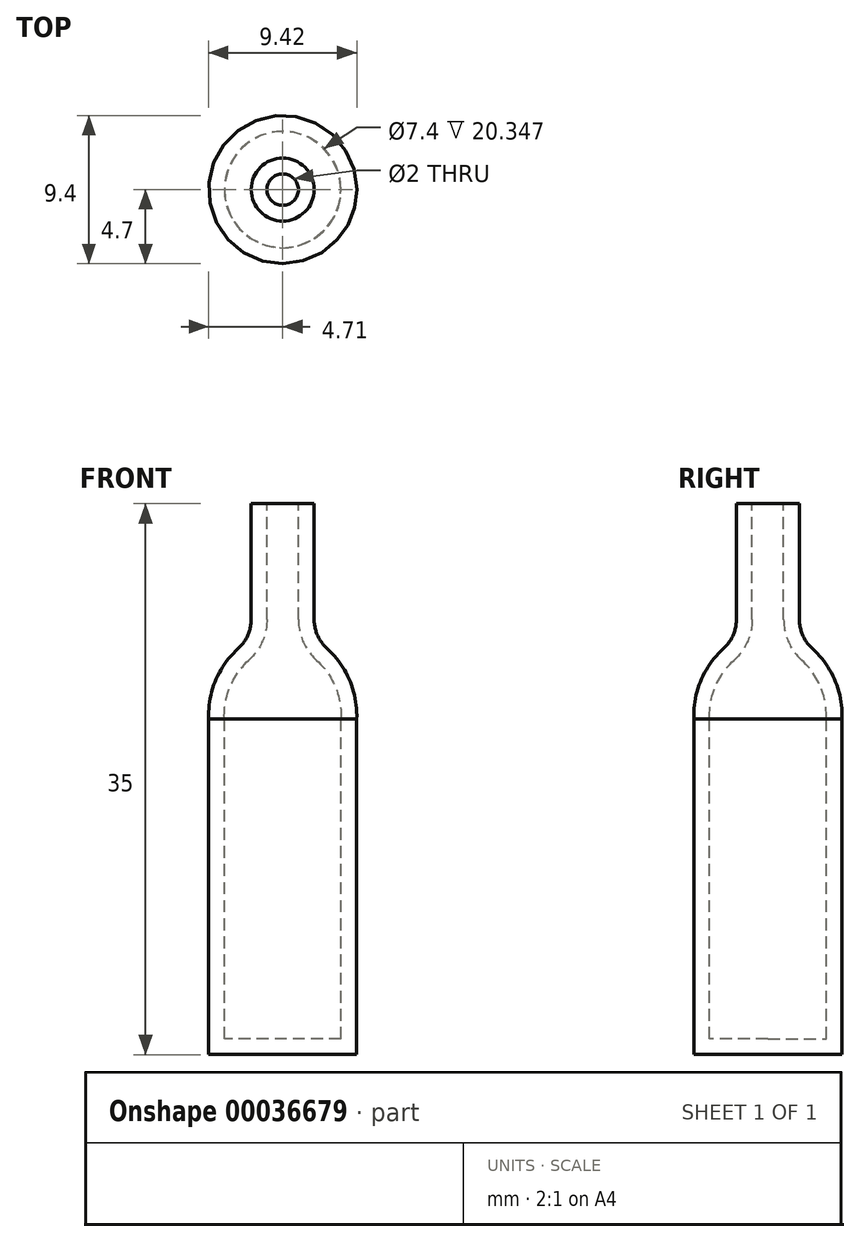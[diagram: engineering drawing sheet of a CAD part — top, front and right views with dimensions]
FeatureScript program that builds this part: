
annotation { "Feature Type Name" : "Feature", "Feature Type Description" : "" }
export const myFeature = defineFeature(function(context is Context, id is Id, definition is map)
    precondition{}
    {
        {
            var Q0;
            Q0=qCreatedBy(makeId("Front.planeOp"),FACE);
            var sketch = newSketch(context, id + "F0", { "sketchPlane" : qUnion([Q0])});
            skLineSegment(sketch, "E0", {"start": v(0, 28.81) * mm, "end": v(-2, 28.81) * mm});
            skLineSegment(sketch, "E1", {"start": v(-2, 27.58) * mm, "end": v(-2, 21.46) * mm});
            skArc(sketch, "E2", {"start": v(-2.82, 19.6) * mm, "mid": v(-4.26, 17.58) * mm, "end": v(-4.7, 15.14) * mm});
            skLineSegment(sketch, "E3", {"start": v(-4.7, 15.14) * mm, "end": v(-4.7, -6.19) * mm});
            skLineSegment(sketch, "E4", {"start": v(-4.7, -6.19) * mm, "end": v(0, -6.19) * mm});
            skLineSegment(sketch, "E5", {"start": v(0, 28.81) * mm, "end": v(0, -6.19) * mm});
            skPoint(sketch, "E6.visualSharp", {"position": v(-2, 20.22) * mm});
            skArc(sketch, "E6.filletArc", {"start": v(-2.82, 19.6) * mm, "mid": v(-2.22, 20.44) * mm, "end": v(-2, 21.46) * mm});
            skLineSegment(sketch, "E7", {"start": v(-2, 27.58) * mm, "end": v(-2, 28.81) * mm});
            skSolve(sketch);
        }
        {
            var Q0;
            Q0=makeQuery(id+"F0.imprint","IMPRINT",FACE,{"disambiguationData":[TD([[makeQuery(id+"F0.imprint","IMPRINT",EDGE,{"derivedFrom":sQuery(id+"F0.wireOp",EDGE,"E0")}),1.0]])]});
            var Q1;
            Q1=sQuery(id+"F0.wireOp",EDGE,"E5");
            revolve(context, id + "F1", {"entities" : qUnion([Q0]), "axis" : qUnion([Q1]), "revolveType" : RevolveType.FULL});
        }
        {
            var Q0;
            Q0=makeQuery(id+"F1.opRevolve","SWEPT_FACE",FACE,{"disambiguationData":[OSD([sQuery(id+"F0.wireOp",EDGE,"E0")])]});
            shell(context, id + "F2", {"entities" : qUnion([Q0]), "thickness" : 1 * mm});
        }
    });
